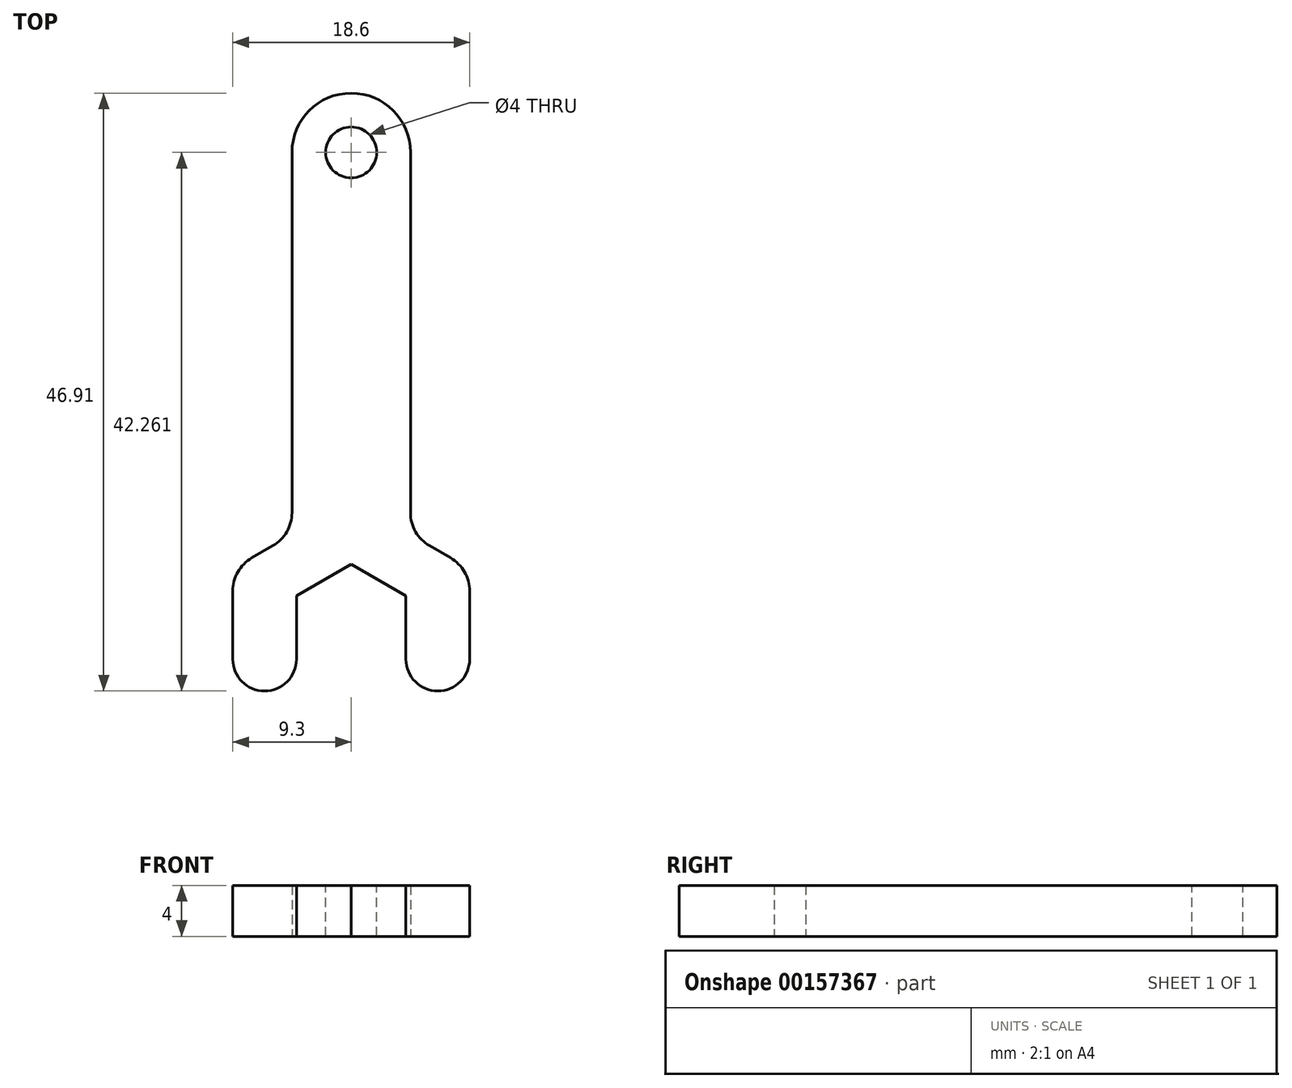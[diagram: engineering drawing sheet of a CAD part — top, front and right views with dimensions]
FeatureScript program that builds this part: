
annotation { "Feature Type Name" : "Feature", "Feature Type Description" : "" }
export const myFeature = defineFeature(function(context is Context, id is Id, definition is map)
    precondition{}
    {
        {
            var Q0;
            Q0=qCreatedBy(makeId("Top.planeOp"),FACE);
            var sketch = newSketch(context, id + "F0", { "sketchPlane" : qUnion([Q0])});
            skCircle(sketch, "E0.cCircle", {"center": v(0, 0) * mm, "radius": 4.3 * mm, "construction": true});
            skLineSegment(sketch, "E0.0", {"start": v(4.3, 2.48) * mm, "end": v(4.3, -2.48) * mm});
            skLineSegment(sketch, "E0.1", {"start": v(4.3, -2.48) * mm, "end": v(0, -4.97) * mm});
            skLineSegment(sketch, "E0.2", {"start": v(0, -4.97) * mm, "end": v(-4.3, -2.48) * mm});
            skLineSegment(sketch, "E0.3", {"start": v(-4.3, -2.48) * mm, "end": v(-4.3, 2.48) * mm});
            skLineSegment(sketch, "E0.4", {"start": v(-4.3, 2.48) * mm, "end": v(0, 4.97) * mm});
            skLineSegment(sketch, "E0.5", {"start": v(0, 4.97) * mm, "end": v(4.3, 2.48) * mm});
            skPoint(sketch, "E0.0.midPoint", {"position": v(4.3, 0) * mm});
            skLineSegment(sketch, "E1", {"start": v(-4.3, -2.48) * mm, "end": v(-9.3, -2.48) * mm});
            skLineSegment(sketch, "E2", {"start": v(0, 4.97) * mm, "end": v(0, 9.97) * mm});
            skLineSegment(sketch, "E3", {"start": v(0, 9.97) * mm, "end": v(-9.3, 4.6) * mm});
            skLineSegment(sketch, "E4", {"start": v(-9.3, 4.6) * mm, "end": v(-9.3, -2.48) * mm});
            skLineSegment(sketch, "E5", {"start": v(4.3, -2.48) * mm, "end": v(9.3, -2.48) * mm});
            skLineSegment(sketch, "E6", {"start": v(0, 9.97) * mm, "end": v(9.3, 4.6) * mm});
            skLineSegment(sketch, "E7", {"start": v(9.3, 4.6) * mm, "end": v(9.3, -2.48) * mm});
            skLineSegment(sketch, "E8", {"start": v(-4.65, 7.28) * mm, "end": v(-4.65, 37.28) * mm});
            skLineSegment(sketch, "E9", {"start": v(4.65, 7.28) * mm, "end": v(4.65, 37.28) * mm});
            skArc(sketch, "E10", {"start": v(4.65, 37.28) * mm, "mid": v(0, 41.93) * mm, "end": v(-4.65, 37.28) * mm});
            skArc(sketch, "E11", {"start": v(-9.3, -2.48) * mm, "mid": v(-6.8, -4.98) * mm, "end": v(-4.3, -2.48) * mm});
            skArc(sketch, "E12", {"start": v(4.3, -2.48) * mm, "mid": v(6.8, -4.98) * mm, "end": v(9.3, -2.48) * mm});
            skPoint(sketch, "E12.midSnap0", {"position": v(6.8, -2.48) * mm});
            skPoint(sketch, "E12.midSnap1", {"position": v(-6.8, -4.98) * mm});
            skSolve(sketch);
        }
        {
            var Q0;
            Q0=makeQuery(id+"F0.imprint","IMPRINT",FACE,{"disambiguationData":[TD([[makeQuery(id+"F0.imprint","IMPRINT",EDGE,{"derivedFrom":sQuery(id+"F0.wireOp",EDGE,"E0.3")}),1.0]])]});
            var Q1;
            Q1=makeQuery(id+"F0.imprint","IMPRINT",FACE,{"disambiguationData":[TD([[makeQuery(id+"F0.imprint","IMPRINT",EDGE,{"derivedFrom":sQuery(id+"F0.wireOp",EDGE,"E0.0")}),1.0]])]});
            var Q2;
            {var subQ4=sQuery(id+"F0.wireOp",EDGE,"E8");Q2=makeQuery(id+"F0.imprint","IMPRINT",FACE,{"disambiguationData":[TD([[makeQuery(id+"F0.imprint","IMPRINT",EDGE,{"derivedFrom":subQ4}),-1.0]])]});}
            var Q3;
            Q3=makeQuery(id+"F0.imprint","IMPRINT",FACE,{"disambiguationData":[TD([[makeQuery(id+"F0.imprint","IMPRINT",EDGE,{"derivedFrom":sQuery(id+"F0.wireOp",EDGE,"E1")}),1.0]])]});
            var Q4;
            Q4=makeQuery(id+"F0.imprint","IMPRINT",FACE,{"disambiguationData":[TD([[makeQuery(id+"F0.imprint","IMPRINT",EDGE,{"derivedFrom":sQuery(id+"F0.wireOp",EDGE,"E5")}),-1.0]])]});
            extrude(context, id + "F1", {"entities" : qUnion([Q0, Q1, Q2, Q3, Q4]), "depth" : 4 * mm});
        }
        {
            var Q0;
            Q0=makeQuery(id+"F1.opExtrude","SWEPT_EDGE",EDGE,{"disambiguationData":[OSD([sQuery(id+"F0.wireOp",EDGE,"E6"),sQuery(id+"F0.wireOp",EDGE,"E7")])]});
            var Q1;
            Q1=makeQuery(id+"F1.opExtrude","SWEPT_EDGE",EDGE,{"disambiguationData":[OSD([sQuery(id+"F0.wireOp",EDGE,"E6"),sQuery(id+"F0.wireOp",EDGE,"E9")])]});
            var Q2;
            Q2=makeQuery(id+"F1.opExtrude","SWEPT_EDGE",EDGE,{"disambiguationData":[OSD([sQuery(id+"F0.wireOp",EDGE,"E3"),sQuery(id+"F0.wireOp",EDGE,"E8")])]});
            var Q3;
            Q3=makeQuery(id+"F1.opExtrude","SWEPT_EDGE",EDGE,{"disambiguationData":[OSD([sQuery(id+"F0.wireOp",EDGE,"E3"),sQuery(id+"F0.wireOp",EDGE,"E4")])]});
            fillet(context, id + "F2", {"entities" : qUnion([Q0, Q1, Q2, Q3]), "radius" : 3 * mm, "tangentPropagation" : true, "allowEdgeOverflow" : false});
        }
        {
            var Q0;
            Q0=makeQuery(id+"F1.opExtrude","CAP_FACE",FACE,{"disambiguationData":[OSD([sQuery(id+"F0.wireOp",EDGE,"E0.0"),sQuery(id+"F0.wireOp",EDGE,"E0.3"),sQuery(id+"F0.wireOp",EDGE,"E0.4"),sQuery(id+"F0.wireOp",EDGE,"E0.5"),sQuery(id+"F0.wireOp",EDGE,"E3"),sQuery(id+"F0.wireOp",EDGE,"E4"),sQuery(id+"F0.wireOp",EDGE,"E6"),sQuery(id+"F0.wireOp",EDGE,"E7"),sQuery(id+"F0.wireOp",EDGE,"E8"),sQuery(id+"F0.wireOp",EDGE,"E9"),sQuery(id+"F0.wireOp",EDGE,"E10"),sQuery(id+"F0.wireOp",EDGE,"E11"),sQuery(id+"F0.wireOp",EDGE,"E12")])],"isStart":false});
            var sketch = newSketch(context, id + "F3", { "sketchPlane" : qUnion([Q0])});
            skCircle(sketch, "E13", {"center": v(0, 37.28) * mm, "radius": 2 * mm});
            skSolve(sketch);
        }
        {
            var Q0;
            Q0=makeQuery(id+"F3.imprint","IMPRINT",FACE,{"disambiguationData":[TD([[makeQuery(id+"F3.imprint","IMPRINT",EDGE,{"derivedFrom":sQuery(id+"F3.wireOp",EDGE,"E13")}),1.0]])]});
            extrude(context, id + "F4", {"entities" : qUnion([Q0]), "operationType" : NewBodyOperationType.REMOVE, "endBound" : BoundingType.UP_TO_NEXT, "oppositeDirection" : true, "depth" : 25 * mm});
        }
    });
